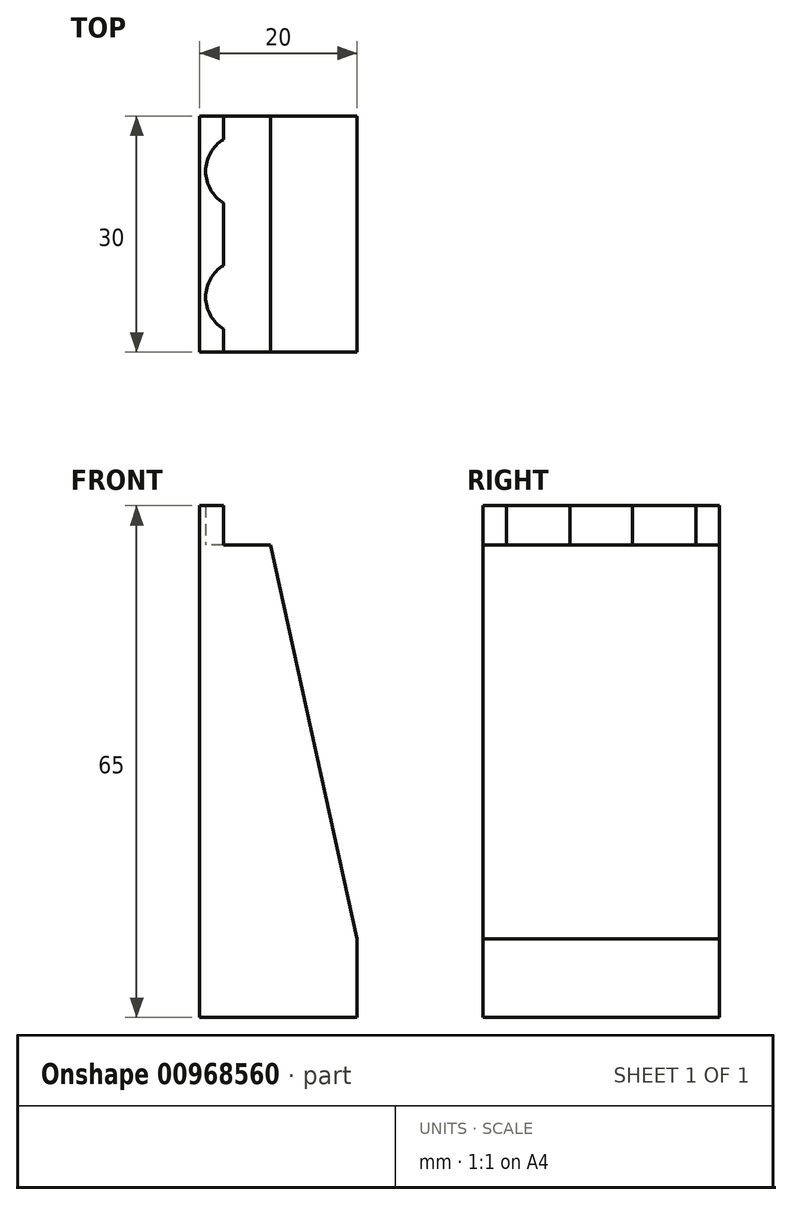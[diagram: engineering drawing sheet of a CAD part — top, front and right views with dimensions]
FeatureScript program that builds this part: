
annotation { "Feature Type Name" : "Feature", "Feature Type Description" : "" }
export const myFeature = defineFeature(function(context is Context, id is Id, definition is map)
    precondition{}
    {
        {
            var Q0;
            Q0=qCreatedBy(makeId("Front.planeOp"),FACE);
            var sketch = newSketch(context, id + "F0", { "sketchPlane" : qUnion([Q0])});
            skLineSegment(sketch, "E0.bottom", {"start": v(0, 0) * mm, "end": v(-20, 0) * mm});
            skLineSegment(sketch, "E0.top", {"start": v(0, 70) * mm, "end": v(-20, 70) * mm});
            skLineSegment(sketch, "E0.left", {"start": v(0, 0) * mm, "end": v(0, 70) * mm});
            skLineSegment(sketch, "E0.right", {"start": v(-20, 0) * mm, "end": v(-20, 70) * mm});
            skSolve(sketch);
        }
        {
            var Q0;
            Q0=makeQuery(id+"F0.imprint","IMPRINT",FACE,{"disambiguationData":[TD([[makeQuery(id+"F0.imprint","IMPRINT",EDGE,{"derivedFrom":sQuery(id+"F0.wireOp",EDGE,"E0.bottom")}),-1.0]])]});
            extrude(context, id + "F1", {"entities" : qUnion([Q0]), "depth" : 30 * mm});
        }
        {
            var Q0;
            Q0=makeQuery(id+"F1.opExtrude","SWEPT_FACE",FACE,{"disambiguationData":[OSD([sQuery(id+"F0.wireOp",EDGE,"E0.right")])]});
            var sketch = newSketch(context, id + "F2", { "sketchPlane" : qUnion([Q0])});
            skLineSegment(sketch, "E1.bottom", {"start": v(0, 0) * mm, "end": v(30, 0) * mm});
            skLineSegment(sketch, "E1.top", {"start": v(0, 10) * mm, "end": v(30, 10) * mm});
            skLineSegment(sketch, "E1.left", {"start": v(0, 0) * mm, "end": v(0, 10) * mm});
            skLineSegment(sketch, "E1.right", {"start": v(30, 0) * mm, "end": v(30, 10) * mm});
            skSolve(sketch);
        }
        {
            var Q0;
            Q0=qSketchRegion(id+"F2",true);
            extrude(context, id + "F3", {"entities" : qUnion([Q0]), "operationType" : NewBodyOperationType.REMOVE, "oppositeDirection" : true, "depth" : 10 * mm});
        }
        {
            var Q0;
            Q0=makeQuery(id+"F3.boolean.opBoolean","COPY",FACE,{"derivedFrom":makeQuery(id+"F3.opExtrude","CAP_FACE",FACE,{"disambiguationData":[OSD([sQuery(id+"F2.wireOp",EDGE,"E1.bottom"),sQuery(id+"F2.wireOp",EDGE,"E1.top"),sQuery(id+"F2.wireOp",EDGE,"E1.left"),sQuery(id+"F2.wireOp",EDGE,"E1.right")])],"isStart":false})});
            var sketch = newSketch(context, id + "F4", { "sketchPlane" : qUnion([Q0])});
            skCircle(sketch, "E2", {"center": v(5, 5) * mm, "radius": 2.05 * mm});
            skCircle(sketch, "E3", {"center": v(25, 5) * mm, "radius": 2.05 * mm});
            skSolve(sketch);
        }
        {
            var Q0;
            Q0=qSketchRegion(id+"F4",true);
            extrude(context, id + "F5", {"entities" : qUnion([Q0]), "operationType" : NewBodyOperationType.REMOVE, "endBound" : BoundingType.UP_TO_NEXT, "oppositeDirection" : true, "depth" : 25 * mm});
        }
        {
            var Q0;
            Q0=makeQuery(id+"F1.opExtrude","SWEPT_FACE",FACE,{"disambiguationData":[OSD([sQuery(id+"F0.wireOp",EDGE,"E0.top")])]});
            var sketch = newSketch(context, id + "F6", { "sketchPlane" : qUnion([Q0])});
            skLineSegment(sketch, "E4.bottom", {"start": v(0, 0) * mm, "end": v(-11, 0) * mm});
            skLineSegment(sketch, "E4.top", {"start": v(0, -30) * mm, "end": v(-11, -30) * mm});
            skLineSegment(sketch, "E4.left", {"start": v(0, 0) * mm, "end": v(0, -30) * mm});
            skLineSegment(sketch, "E4.right", {"start": v(-11, 0) * mm, "end": v(-11, -30) * mm});
            skSolve(sketch);
        }
        {
            var Q0;
            Q0=qSketchRegion(id+"F6",true);
            extrude(context, id + "F7", {"entities" : qUnion([Q0]), "operationType" : NewBodyOperationType.REMOVE, "oppositeDirection" : true, "depth" : 50 * mm});
        }
        {
            var Q0;
            Q0=makeQuery(id+"F1.opExtrude","SWEPT_FACE",FACE,{"disambiguationData":[OSD([sQuery(id+"F0.wireOp",EDGE,"E0.top")])]});
            var sketch = newSketch(context, id + "F8", { "sketchPlane" : qUnion([Q0])});
            skLineSegment(sketch, "E5", {"start": v(-37.78, -15) * mm, "end": v(17.7, -15) * mm, "construction": true});
            skLineSegment(sketch, "E6", {"start": v(-30.22, -7) * mm, "end": v(11.91, -7) * mm, "construction": true});
            skLineSegment(sketch, "E7", {"start": v(-33.53, -23) * mm, "end": v(14.63, -23) * mm, "construction": true});
            skLineSegment(sketch, "E8", {"start": v(-14.5, 4.82) * mm, "end": v(-14.5, -41.88) * mm, "construction": true});
            skArc(sketch, "E9", {"start": v(-17, -2.96) * mm, "mid": v(-19.25, -7) * mm, "end": v(-17, -11.04) * mm, "construction": true});
            skArc(sketch, "E10", {"start": v(-17, -18.96) * mm, "mid": v(-19.25, -23) * mm, "end": v(-17, -27.04) * mm, "construction": true});
            skLineSegment(sketch, "E11", {"start": v(-17, 19.13) * mm, "end": v(-17, -11.04) * mm, "construction": true});
            skLineSegment(sketch, "E12", {"start": v(-17, -2.96) * mm, "end": v(-17, 0) * mm});
            skLineSegment(sketch, "E13", {"start": v(-17, 0) * mm, "end": v(-20, 0) * mm});
            skLineSegment(sketch, "E14", {"start": v(-20, 0) * mm, "end": v(-20, -30) * mm});
            skLineSegment(sketch, "E15", {"start": v(-20, -30) * mm, "end": v(-17, -30) * mm});
            skLineSegment(sketch, "E16", {"start": v(-17, -30) * mm, "end": v(-17, -27.04) * mm});
            skLineSegment(sketch, "E17", {"start": v(-17, -18.96) * mm, "end": v(-17, -11.04) * mm});
            skPoint(sketch, "E18", {"position": v(-19.25, -7) * mm});
            skPoint(sketch, "E19", {"position": v(-19.25, -23) * mm});
            skArc(sketch, "E20", {"start": v(-17, -2.96) * mm, "mid": v(-19.25, -7) * mm, "end": v(-17, -11.04) * mm});
            skArc(sketch, "E21", {"start": v(-17, -18.96) * mm, "mid": v(-19.25, -23) * mm, "end": v(-17, -27.04) * mm});
            skLineSegment(sketch, "E22", {"start": v(-17, -11.04) * mm, "end": v(-17, -48.69) * mm, "construction": true});
            skSolve(sketch);
        }
        {
            var Q0;
            Q0=qSketchRegion(id+"F8",true);
            extrude(context, id + "F9", {"entities" : qUnion([Q0]), "operationType" : NewBodyOperationType.ADD, "depth" : 5 * mm});
        }
        {
            var Q0;
            Q0=makeQuery(id+"F7.boolean.opBoolean","COPY",EDGE,{"derivedFrom":makeQuery(id+"F7.opExtrude","CAP_EDGE",EDGE,{"disambiguationData":[OSD([sQuery(id+"F6.wireOp",EDGE,"E4.right")])],"isStart":false})});
            chamfer(context, id + "F10", {"entities" : qUnion([Q0]), "chamferType" : ChamferType.TWO_OFFSETS, "width1" : 11 * mm, "oppositeDirection" : false, "width2" : 50 * mm, "tangentPropagation" : true});
        }
        {
            var Q0;
            Q0=makeQuery(id+"F3.boolean.opBoolean","COPY",FACE,{"derivedFrom":makeQuery(id+"F3.opExtrude","CAP_FACE",FACE,{"disambiguationData":[OSD([sQuery(id+"F2.wireOp",EDGE,"E1.bottom"),sQuery(id+"F2.wireOp",EDGE,"E1.top"),sQuery(id+"F2.wireOp",EDGE,"E1.left"),sQuery(id+"F2.wireOp",EDGE,"E1.right")])],"isStart":false})});
            var sketch = newSketch(context, id + "F11", { "sketchPlane" : qUnion([Q0])});
            skLineSegment(sketch, "E23.0.0", {"start": v(30, 10) * mm, "end": v(0, 10) * mm});
            skLineSegment(sketch, "E23.0.1", {"start": v(0, 10) * mm, "end": v(0, 0) * mm});
            skLineSegment(sketch, "E23.0.2", {"start": v(0, 0) * mm, "end": v(30, 0) * mm});
            skLineSegment(sketch, "E23.0.3", {"start": v(30, 0) * mm, "end": v(30, 10) * mm});
            skSolve(sketch);
        }
        {
            var Q0;
            Q0=qSketchRegion(id+"F11",true);
            extrude(context, id + "F12", {"entities" : qUnion([Q0]), "operationType" : NewBodyOperationType.REMOVE, "oppositeDirection" : true, "depth" : 25 * mm, "offsetDistance" : 25 * mm});
        }
    });
